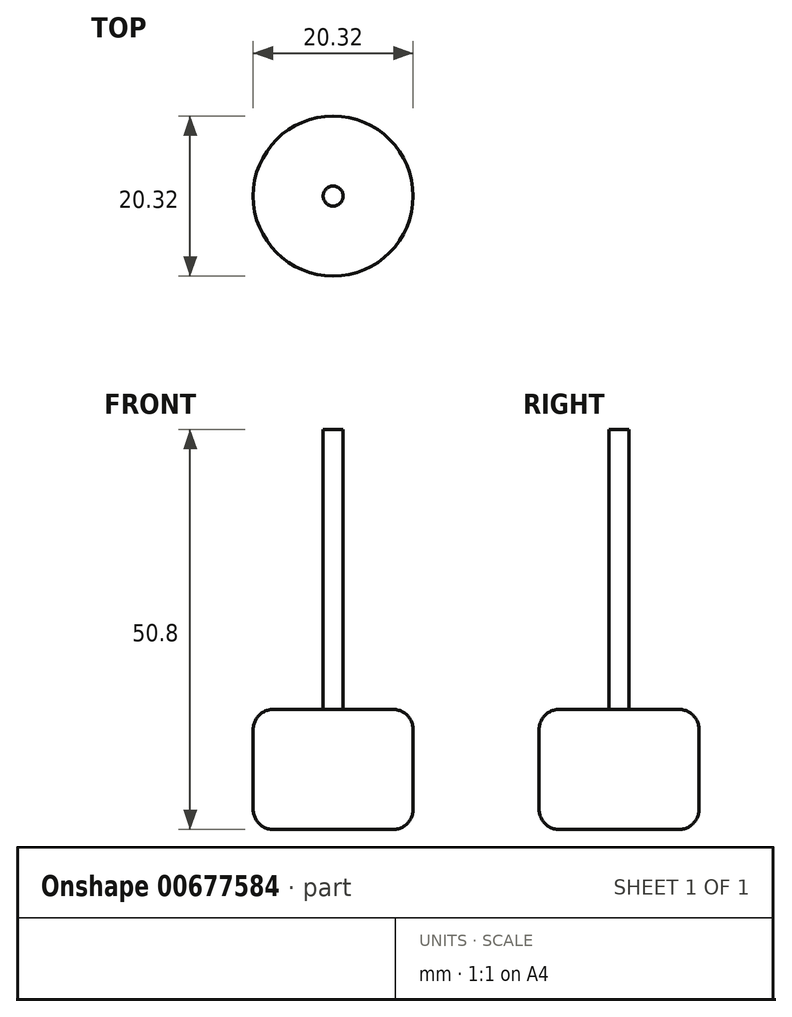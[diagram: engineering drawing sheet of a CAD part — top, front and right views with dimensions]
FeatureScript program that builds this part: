
annotation { "Feature Type Name" : "Feature", "Feature Type Description" : "" }
export const myFeature = defineFeature(function(context is Context, id is Id, definition is map)
    precondition{}
    {
        {
            var Q0;
            Q0=qCreatedBy(makeId("Top.planeOp"),FACE);
            var sketch = newSketch(context, id + "F0", { "sketchPlane" : qUnion([Q0])});
            skCircle(sketch, "E0", {"center": v(0, 0) * mm, "radius": 10.16 * mm});
            skSolve(sketch);
        }
        {
            var Q0;
            Q0=makeQuery(id+"F0.imprint","IMPRINT",FACE,{"disambiguationData":[TD([[makeQuery(id+"F0.imprint","IMPRINT",EDGE,{"derivedFrom":sQuery(id+"F0.wireOp",EDGE,"E0")}),1.0]])]});
            extrude(context, id + "F1", {"entities" : qUnion([Q0]), "depth" : 15.24 * mm, "offsetDistance" : 25.4 * mm});
        }
        {
            var Q0;
            Q0=makeQuery(id+"F1.opExtrude","CAP_EDGE",EDGE,{"disambiguationData":[OSD([sQuery(id+"F0.wireOp",EDGE,"E0")])],"isStart":false});
            var Q1;
            Q1=makeQuery(id+"F1.opExtrude","CAP_EDGE",EDGE,{"disambiguationData":[OSD([sQuery(id+"F0.wireOp",EDGE,"E0")])],"isStart":true});
            fillet(context, id + "F2", {"entities" : qUnion([Q0, Q1]), "radius" : 2.54 * mm, "tangentPropagation" : true, "allowEdgeOverflow" : false});
        }
        {
            var Q0;
            Q0=makeQuery(id+"F1.opExtrude","CAP_FACE",FACE,{"disambiguationData":[OSD([sQuery(id+"F0.wireOp",EDGE,"E0")])],"isStart":false});
            var sketch = newSketch(context, id + "F3", { "sketchPlane" : qUnion([Q0])});
            skCircle(sketch, "E1", {"center": v(0, 0) * mm, "radius": 1.27 * mm});
            skSolve(sketch);
        }
        {
            var Q0;
            Q0 = qSketchRegion(id + "F3", true);
            extrude(context, id + "F4", {"entities" : qUnion([Q0]), "operationType" : NewBodyOperationType.ADD, "depth" : 35.56 * mm, "offsetDistance" : 25.4 * mm});
        }
    });
